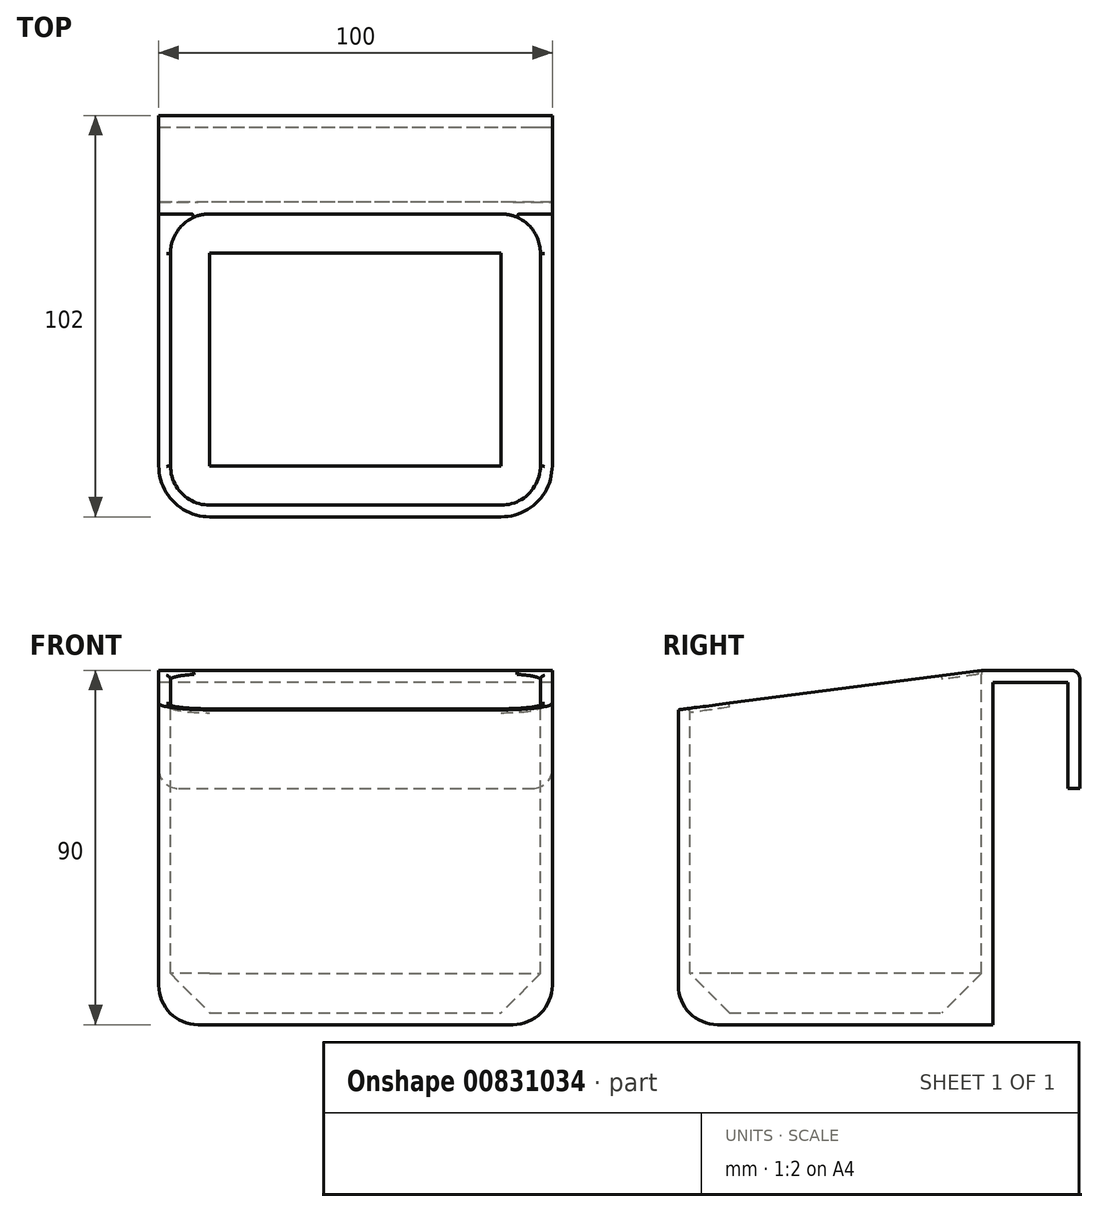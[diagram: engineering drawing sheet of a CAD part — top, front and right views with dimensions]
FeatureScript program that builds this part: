
annotation { "Feature Type Name" : "Feature", "Feature Type Description" : "" }
export const myFeature = defineFeature(function(context is Context, id is Id, definition is map)
    precondition{}
    {
        {
            var Q0;
            Q0=qCreatedBy(makeId("Top.planeOp"),FACE);
            var sketch = newSketch(context, id + "F0", { "sketchPlane" : qUnion([Q0])});
            skLineSegment(sketch, "E0.bottom", {"start": v(50, 40) * mm, "end": v(-50, 40) * mm});
            skLineSegment(sketch, "E0.top", {"start": v(50, -40) * mm, "end": v(-50, -40) * mm});
            skLineSegment(sketch, "E0.left", {"start": v(50, 40) * mm, "end": v(50, -40) * mm});
            skLineSegment(sketch, "E0.right", {"start": v(-50, 40) * mm, "end": v(-50, -40) * mm});
            skPoint(sketch, "E0.middle", {"position": v(0, 0) * mm});
            skLineSegment(sketch, "E1", {"start": v(-50, 40) * mm, "end": v(-50, 59) * mm});
            skLineSegment(sketch, "E2", {"start": v(50, 40) * mm, "end": v(50, 59) * mm});
            skLineSegment(sketch, "E3", {"start": v(-50, 59) * mm, "end": v(50, 59) * mm});
            skLineSegment(sketch, "E4", {"start": v(-50, 59) * mm, "end": v(-50, 61) * mm});
            skLineSegment(sketch, "E5", {"start": v(50, 59) * mm, "end": v(50, 61) * mm});
            skLineSegment(sketch, "E6", {"start": v(50, 61) * mm, "end": v(-50, 61) * mm});
            skSolve(sketch);
        }
        {
            var Q0;
            Q0=makeQuery(id+"F0.imprint","IMPRINT",FACE,{"disambiguationData":[TD([[makeQuery(id+"F0.imprint","IMPRINT",EDGE,{"derivedFrom":sQuery(id+"F0.wireOp",EDGE,"E0.bottom")}),1.0]])]});
            extrude(context, id + "F1", {"entities" : qUnion([Q0]), "depth" : 90 * mm, "offsetDistance" : 25 * mm});
        }
        {
            var Q0;
            Q0=makeQuery(id+"F1.opExtrude","CAP_FACE",FACE,{"disambiguationData":[OSD([sQuery(id+"F0.wireOp",EDGE,"E0.bottom"),sQuery(id+"F0.wireOp",EDGE,"E0.top"),sQuery(id+"F0.wireOp",EDGE,"E0.left"),sQuery(id+"F0.wireOp",EDGE,"E0.right")])],"isStart":false});
            var sketch = newSketch(context, id + "F2", { "sketchPlane" : qUnion([Q0])});
            skLineSegment(sketch, "E7", {"start": v(50, 40) * mm, "end": v(50, 59) * mm});
            skLineSegment(sketch, "E8", {"start": v(-50, 40) * mm, "end": v(-50, 59) * mm});
            skLineSegment(sketch, "E9", {"start": v(-50, 59) * mm, "end": v(50, 59) * mm});
            skLineSegment(sketch, "E10", {"start": v(-50, 59) * mm, "end": v(-50, 62) * mm});
            skLineSegment(sketch, "E11", {"start": v(50, 59) * mm, "end": v(50, 62) * mm});
            skLineSegment(sketch, "E12", {"start": v(-50, 62) * mm, "end": v(50, 62) * mm});
            skSolve(sketch);
        }
        {
            var Q0;
            Q0=makeQuery(id+"F2.imprint","IMPRINT",FACE,{"disambiguationData":[TD([[makeQuery(id+"F2.imprint","IMPRINT",EDGE,{"derivedFrom":sQuery(id+"F2.wireOp",EDGE,"E7")}),1.0]])]});
            extrude(context, id + "F3", {"entities" : qUnion([Q0]), "operationType" : NewBodyOperationType.ADD, "depth" : -3 * mm, "offsetDistance" : 25 * mm});
        }
        {
            var Q0;
            Q0 = qSketchRegion(id + "F2", true);
            var Q1;
            Q1=makeQuery(id+"F2.imprint","IMPRINT",FACE,{"disambiguationData":[TD([[makeQuery(id+"F2.imprint","IMPRINT",EDGE,{"derivedFrom":sQuery(id+"F2.wireOp",EDGE,"E9")}),1.0]])]});
            extrude(context, id + "F4", {"entities" : qUnion([Q0, Q1]), "operationType" : NewBodyOperationType.ADD, "depth" : -30 * mm, "offsetDistance" : 25 * mm});
        }
        {
            var Q0;
            Q0=makeQuery(id+"F2.imprint","IMPRINT",FACE,{"disambiguationData":[TD([[makeQuery(id+"F2.imprint","IMPRINT",EDGE,{"derivedFrom":makeQuery(id+"F1.opExtrude","CAP_EDGE",EDGE,{"disambiguationData":[OSD([sQuery(id+"F0.wireOp",EDGE,"E0.bottom")])],"isStart":false})}),1.0]])]});
            var sketch = newSketch(context, id + "F5", { "sketchPlane" : qUnion([Q0])});
            skLineSegment(sketch, "E13.bottom", {"start": v(47, 37) * mm, "end": v(-47, 37) * mm});
            skLineSegment(sketch, "E13.top", {"start": v(47, -37) * mm, "end": v(-47, -37) * mm});
            skLineSegment(sketch, "E13.left", {"start": v(47, 37) * mm, "end": v(47, -37) * mm});
            skLineSegment(sketch, "E13.right", {"start": v(-47, 37) * mm, "end": v(-47, -37) * mm});
            skPoint(sketch, "E13.middle", {"position": v(0, 0) * mm});
            skSolve(sketch);
        }
        {
            var Q0;
            Q0=makeQuery(id+"F5.imprint","IMPRINT",FACE,{"disambiguationData":[TD([[makeQuery(id+"F5.imprint","IMPRINT",EDGE,{"derivedFrom":sQuery(id+"F5.wireOp",EDGE,"E13.bottom")}),1.0]])]});
            extrude(context, id + "F6", {"entities" : qUnion([Q0]), "operationType" : NewBodyOperationType.REMOVE, "oppositeDirection" : true, "depth" : 87 * mm, "offsetDistance" : 25 * mm});
        }
        {
            var Q0;
            Q0=makeQuery(id+"F4.boolean.opBoolean","MERGE",FACE,{"derivedFrom":[makeQuery(id+"F3.boolean.opBoolean","MERGE",FACE,{"derivedFrom":[makeQuery(id+"F1.opExtrude","SWEPT_FACE",FACE,{"disambiguationData":[OSD([sQuery(id+"F0.wireOp",EDGE,"E0.left")])]}),makeQuery(id+"F3.opExtrude","SWEPT_FACE",FACE,{"disambiguationData":[OSD([sQuery(id+"F2.wireOp",EDGE,"E7")])]})]}),makeQuery(id+"F4.opExtrude","SWEPT_FACE",FACE,{"disambiguationData":[OSD([sQuery(id+"F2.wireOp",EDGE,"E11")])]})]});
            var sketch = newSketch(context, id + "F7", { "sketchPlane" : qUnion([Q0])});
            skLineSegment(sketch, "E14", {"start": v(-40, 90) * mm, "end": v(-40, 80) * mm});
            skLineSegment(sketch, "E15", {"start": v(-40, 80) * mm, "end": v(37, 90) * mm});
            skLineSegment(sketch, "E16", {"start": v(37, 90) * mm, "end": v(-40, 90) * mm});
            skSolve(sketch);
        }
        {
            var Q0;
            Q0=makeQuery(id+"F7.imprint","IMPRINT",FACE,{"disambiguationData":[TD([[makeQuery(id+"F7.imprint","IMPRINT",EDGE,{"derivedFrom":sQuery(id+"F7.wireOp",EDGE,"E14")}),1.0]])]});
            extrude(context, id + "F8", {"entities" : qUnion([Q0]), "operationType" : NewBodyOperationType.REMOVE, "oppositeDirection" : true, "depth" : 100 * mm, "offsetDistance" : 25 * mm});
        }
        {
            var Q0;
            Q0=makeQuery(id+"F6.boolean.opBoolean","COPY",EDGE,{"derivedFrom":makeQuery(id+"F6.opExtrude","SWEPT_EDGE",EDGE,{"disambiguationData":[OSD([sQuery(id+"F5.wireOp",EDGE,"E13.bottom"),sQuery(id+"F5.wireOp",EDGE,"E13.left")])]})});
            var Q1;
            Q1=makeQuery(id+"F6.boolean.opBoolean","COPY",EDGE,{"derivedFrom":makeQuery(id+"F6.opExtrude","SWEPT_EDGE",EDGE,{"disambiguationData":[OSD([sQuery(id+"F5.wireOp",EDGE,"E13.top"),sQuery(id+"F5.wireOp",EDGE,"E13.left")])]})});
            var Q2;
            Q2=makeQuery(id+"F6.boolean.opBoolean","COPY",EDGE,{"derivedFrom":makeQuery(id+"F6.opExtrude","SWEPT_EDGE",EDGE,{"disambiguationData":[OSD([sQuery(id+"F5.wireOp",EDGE,"E13.top"),sQuery(id+"F5.wireOp",EDGE,"E13.right")])]})});
            var Q3;
            Q3=makeQuery(id+"F6.boolean.opBoolean","COPY",EDGE,{"derivedFrom":makeQuery(id+"F6.opExtrude","SWEPT_EDGE",EDGE,{"disambiguationData":[OSD([sQuery(id+"F5.wireOp",EDGE,"E13.bottom"),sQuery(id+"F5.wireOp",EDGE,"E13.right")])]})});
            fillet(context, id + "F9", {"entities" : qUnion([Q0, Q1, Q2, Q3]), "radius" : 10 * mm, "tangentPropagation" : true, "allowEdgeOverflow" : false});
        }
        {
            var Q0;
            Q0=makeQuery(id+"F6.boolean.opBoolean","COPY",EDGE,{"derivedFrom":makeQuery(id+"F6.opExtrude","CAP_EDGE",EDGE,{"disambiguationData":[OSD([sQuery(id+"F5.wireOp",EDGE,"E13.right")])],"isStart":false})});
            chamfer(context, id + "F10", {"entities" : qUnion([Q0]), "width" : 10 * mm, "tangentPropagation" : true});
        }
        {
            var Q0;
            Q0=makeQuery(id+"F1.opExtrude","SWEPT_EDGE",EDGE,{"disambiguationData":[OSD([sQuery(id+"F0.wireOp",EDGE,"E0.top"),sQuery(id+"F0.wireOp",EDGE,"E0.right")])]});
            var Q1;
            Q1=makeQuery(id+"F1.opExtrude","SWEPT_EDGE",EDGE,{"disambiguationData":[OSD([sQuery(id+"F0.wireOp",EDGE,"E0.top"),sQuery(id+"F0.wireOp",EDGE,"E0.left")])]});
            fillet(context, id + "F11", {"entities" : qUnion([Q0, Q1]), "radius" : 13 * mm, "tangentPropagation" : true, "allowEdgeOverflow" : false});
        }
        {
            var Q0;
            Q0=makeQuery(id+"F1.opExtrude","CAP_EDGE",EDGE,{"disambiguationData":[OSD([sQuery(id+"F0.wireOp",EDGE,"E0.top")])],"isStart":true});
            fillet(context, id + "F12", {"entities" : qUnion([Q0]), "radius" : 10 * mm, "tangentPropagation" : true, "allowEdgeOverflow" : false});
        }
        {
            var Q0;
            Q0=makeQuery(id+"F4.opExtrude","CAP_EDGE",EDGE,{"disambiguationData":[OSD([sQuery(id+"F2.wireOp",EDGE,"E11")])],"isStart":false});
            var Q1;
            Q1=makeQuery(id+"F4.opExtrude","CAP_EDGE",EDGE,{"disambiguationData":[OSD([sQuery(id+"F2.wireOp",EDGE,"E10")])],"isStart":false});
            fillet(context, id + "F13", {"entities" : qUnion([Q0, Q1]), "radius" : 5 * mm, "tangentPropagation" : true, "allowEdgeOverflow" : false});
        }
        {
            var Q0;
            Q0=makeQuery(id+"F4.opExtrude","CAP_EDGE",EDGE,{"disambiguationData":[OSD([sQuery(id+"F2.wireOp",EDGE,"E12")])],"isStart":true});
            fillet(context, id + "F14", {"entities" : qUnion([Q0]), "radius" : 2 * mm, "tangentPropagation" : true, "allowEdgeOverflow" : false});
        }
        {
            var Q0;
            Q0=makeQuery(id+"F8.boolean.opBoolean","INTERSECT",EDGE,{"derivedFrom":[makeQuery(id+"F6.boolean.opBoolean","COPY",FACE,{"derivedFrom":makeQuery(id+"F6.opExtrude","SWEPT_FACE",FACE,{"disambiguationData":[OSD([sQuery(id+"F5.wireOp",EDGE,"E13.left")])]})}),makeQuery(id+"F8.opExtrude","SWEPT_FACE",FACE,{"disambiguationData":[OSD([sQuery(id+"F7.wireOp",EDGE,"E15")])]})]});
            var Q1;
            Q1=makeQuery(id+"F6.boolean.opBoolean","COPY",EDGE,{"derivedFrom":makeQuery(id+"F6.opExtrude","CAP_EDGE",EDGE,{"disambiguationData":[OSD([sQuery(id+"F5.wireOp",EDGE,"E13.bottom")])],"isStart":true})});
            var Q2;
            Q2=makeQuery(id+"F8.boolean.opBoolean","INTERSECT",EDGE,{"derivedFrom":[makeQuery(id+"F6.boolean.opBoolean","COPY",FACE,{"derivedFrom":makeQuery(id+"F6.opExtrude","SWEPT_FACE",FACE,{"disambiguationData":[OSD([sQuery(id+"F5.wireOp",EDGE,"E13.right")])]})}),makeQuery(id+"F8.opExtrude","SWEPT_FACE",FACE,{"disambiguationData":[OSD([sQuery(id+"F7.wireOp",EDGE,"E15")])]})]});
            var Q3;
            Q3=makeQuery(id+"F8.boolean.opBoolean","INTERSECT",EDGE,{"derivedFrom":[makeQuery(id+"F6.boolean.opBoolean","COPY",FACE,{"derivedFrom":makeQuery(id+"F6.opExtrude","SWEPT_FACE",FACE,{"disambiguationData":[OSD([sQuery(id+"F5.wireOp",EDGE,"E13.top")])]})}),makeQuery(id+"F8.opExtrude","SWEPT_FACE",FACE,{"disambiguationData":[OSD([sQuery(id+"F7.wireOp",EDGE,"E15")])]})]});
            var Q4;
            Q4=makeQuery(id+"F9.opFillet","BLEND_EDGE",EDGE,{"blendedFrom":[makeQuery(id+"F6.boolean.opBoolean","COPY",EDGE,{"derivedFrom":makeQuery(id+"F6.opExtrude","SWEPT_EDGE",EDGE,{"disambiguationData":[OSD([sQuery(id+"F5.wireOp",EDGE,"E13.bottom"),sQuery(id+"F5.wireOp",EDGE,"E13.left")])]})}),makeQuery(id+"F8.boolean.opBoolean","COPY",FACE,{"derivedFrom":makeQuery(id+"F8.opExtrude","SWEPT_FACE",FACE,{"disambiguationData":[OSD([sQuery(id+"F7.wireOp",EDGE,"E15")])]})})],"blendedInto":[makeQuery(id+"F8.boolean.opBoolean","COPY",FACE,{"derivedFrom":makeQuery(id+"F8.opExtrude","SWEPT_FACE",FACE,{"disambiguationData":[OSD([sQuery(id+"F7.wireOp",EDGE,"E15")])]})})]});
            var Q5;
            Q5=makeQuery(id+"F9.opFillet","BLEND_EDGE",EDGE,{"blendedFrom":[makeQuery(id+"F6.boolean.opBoolean","COPY",EDGE,{"derivedFrom":makeQuery(id+"F6.opExtrude","SWEPT_EDGE",EDGE,{"disambiguationData":[OSD([sQuery(id+"F5.wireOp",EDGE,"E13.top"),sQuery(id+"F5.wireOp",EDGE,"E13.right")])]})}),makeQuery(id+"F8.boolean.opBoolean","COPY",FACE,{"derivedFrom":makeQuery(id+"F8.opExtrude","SWEPT_FACE",FACE,{"disambiguationData":[OSD([sQuery(id+"F7.wireOp",EDGE,"E15")])]})})],"blendedInto":[makeQuery(id+"F8.boolean.opBoolean","COPY",FACE,{"derivedFrom":makeQuery(id+"F8.opExtrude","SWEPT_FACE",FACE,{"disambiguationData":[OSD([sQuery(id+"F7.wireOp",EDGE,"E15")])]})})]});
            var Q6;
            Q6=makeQuery(id+"F9.opFillet","BLEND_EDGE",EDGE,{"blendedFrom":[makeQuery(id+"F6.boolean.opBoolean","COPY",EDGE,{"derivedFrom":makeQuery(id+"F6.opExtrude","SWEPT_EDGE",EDGE,{"disambiguationData":[OSD([sQuery(id+"F5.wireOp",EDGE,"E13.top"),sQuery(id+"F5.wireOp",EDGE,"E13.left")])]})}),makeQuery(id+"F8.boolean.opBoolean","COPY",FACE,{"derivedFrom":makeQuery(id+"F8.opExtrude","SWEPT_FACE",FACE,{"disambiguationData":[OSD([sQuery(id+"F7.wireOp",EDGE,"E15")])]})})],"blendedInto":[makeQuery(id+"F8.boolean.opBoolean","COPY",FACE,{"derivedFrom":makeQuery(id+"F8.opExtrude","SWEPT_FACE",FACE,{"disambiguationData":[OSD([sQuery(id+"F7.wireOp",EDGE,"E15")])]})})]});
            var Q7;
            Q7=makeQuery(id+"F9.opFillet","BLEND_EDGE",EDGE,{"blendedFrom":[makeQuery(id+"F6.boolean.opBoolean","COPY",EDGE,{"derivedFrom":makeQuery(id+"F6.opExtrude","SWEPT_EDGE",EDGE,{"disambiguationData":[OSD([sQuery(id+"F5.wireOp",EDGE,"E13.bottom"),sQuery(id+"F5.wireOp",EDGE,"E13.right")])]})}),makeQuery(id+"F8.boolean.opBoolean","COPY",FACE,{"derivedFrom":makeQuery(id+"F8.opExtrude","SWEPT_FACE",FACE,{"disambiguationData":[OSD([sQuery(id+"F7.wireOp",EDGE,"E15")])]})})],"blendedInto":[makeQuery(id+"F8.boolean.opBoolean","COPY",FACE,{"derivedFrom":makeQuery(id+"F8.opExtrude","SWEPT_FACE",FACE,{"disambiguationData":[OSD([sQuery(id+"F7.wireOp",EDGE,"E15")])]})})]});
            fillet(context, id + "F15", {"entities" : qUnion([Q0, Q1, Q2, Q3, Q4, Q5, Q6, Q7]), "radius" : 1 * mm, "tangentPropagation" : true, "allowEdgeOverflow" : false});
        }
    });
